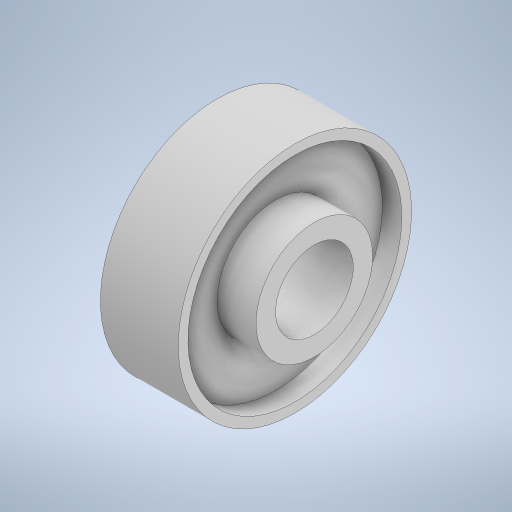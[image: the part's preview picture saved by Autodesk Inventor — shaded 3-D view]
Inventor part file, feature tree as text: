
AUTODESK INVENTOR PART (.ipt)
format: ipt  version: 2024 (Build 280153000, 153)  size: 278,528 bytes
history: native  units: mm
features: other x1, revolve x1, sketch x1
ambient origin geometry x8: Origin, YZ Plane, XZ Plane, XY Plane, X Axis, Y Axis, Z Axis, Center Point
bodies: Body1 (feature_tree)
feature tree (3):
  other  "Sólido1"
  revolve  "Revolución1"  [1 undecoded]
  sketch  "Boceto1"  dims[d6=30.0mm d7=20.0mm d8=5.0mm d9=60.0mm d10=55.0mm d11=30.0mm d12=20.0mm d13=90.0deg]
note: 1 required parameter value undecoded (feature->parameter linkage not recoverable at this tier; creation-order binding heuristic only, values carry confidence <= 0.55)
